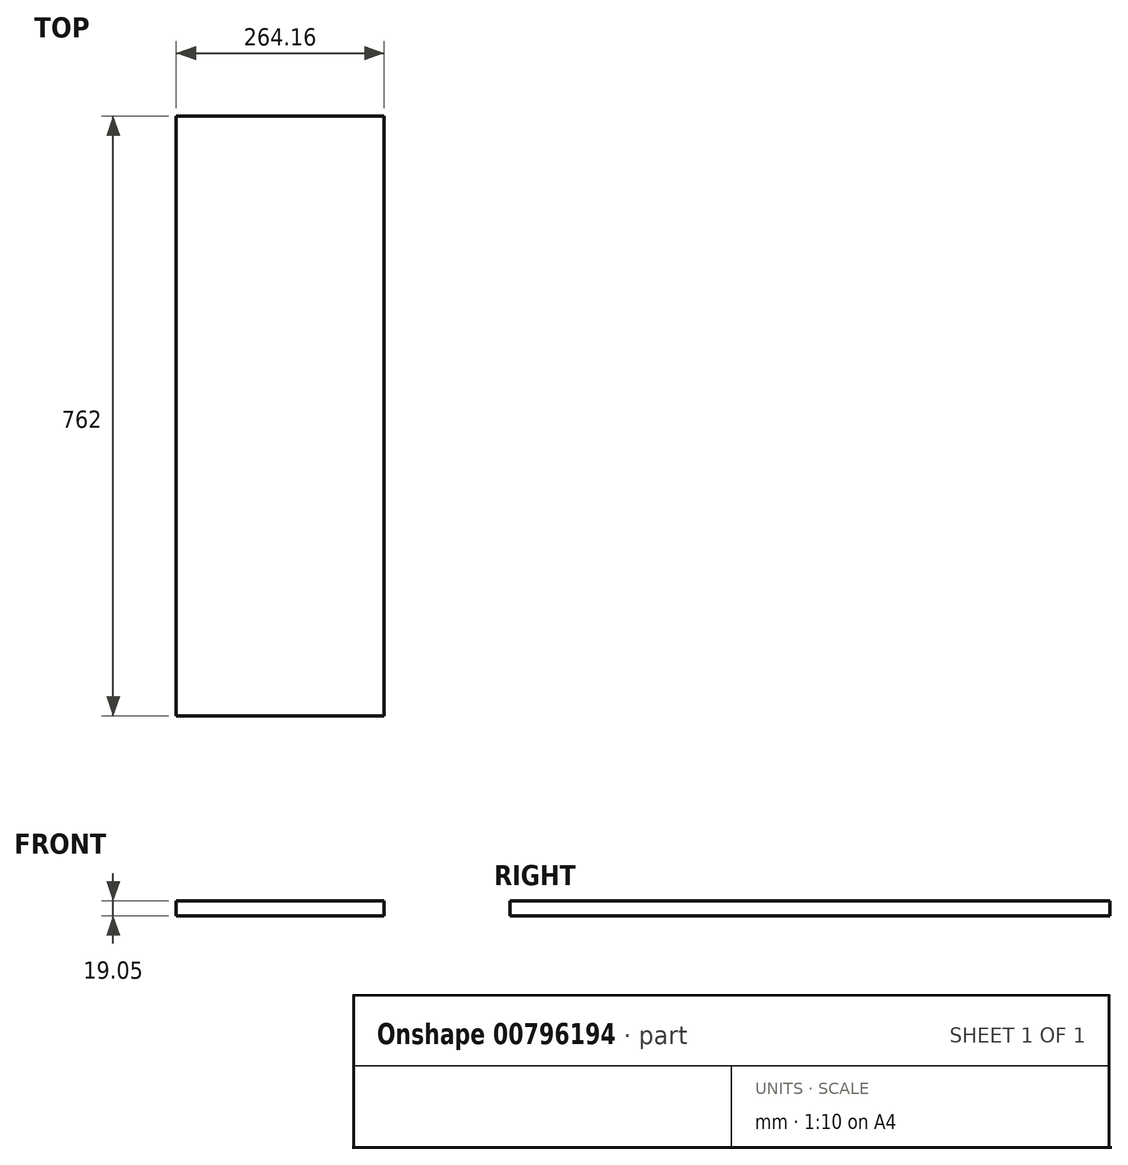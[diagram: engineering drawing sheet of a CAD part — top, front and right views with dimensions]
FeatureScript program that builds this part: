
annotation { "Feature Type Name" : "Feature", "Feature Type Description" : "" }
export const myFeature = defineFeature(function(context is Context, id is Id, definition is map)
    precondition{}
    {
        {
            var Q0;
            Q0=qCreatedBy(makeId("Top.planeOp"),FACE);
            var sketch = newSketch(context, id + "F0", { "sketchPlane" : qUnion([Q0])});
            skLineSegment(sketch, "E0.bottom", {"start": v(-132.08, 381) * mm, "end": v(132.08, 381) * mm});
            skLineSegment(sketch, "E0.top", {"start": v(-132.08, -381) * mm, "end": v(132.08, -381) * mm});
            skLineSegment(sketch, "E0.left", {"start": v(-132.08, 381) * mm, "end": v(-132.08, -381) * mm});
            skLineSegment(sketch, "E0.right", {"start": v(132.08, 381) * mm, "end": v(132.08, -381) * mm});
            skPoint(sketch, "E0.middle", {"position": v(0, 0) * mm});
            skSolve(sketch);
        }
        {
            var Q0;
            Q0=qSketchRegion(id+"F0",true);
            extrude(context, id + "F1", {"entities" : qUnion([Q0]), "depth" : 19.05 * mm, "offsetDistance" : 25.4 * mm});
        }
    });
